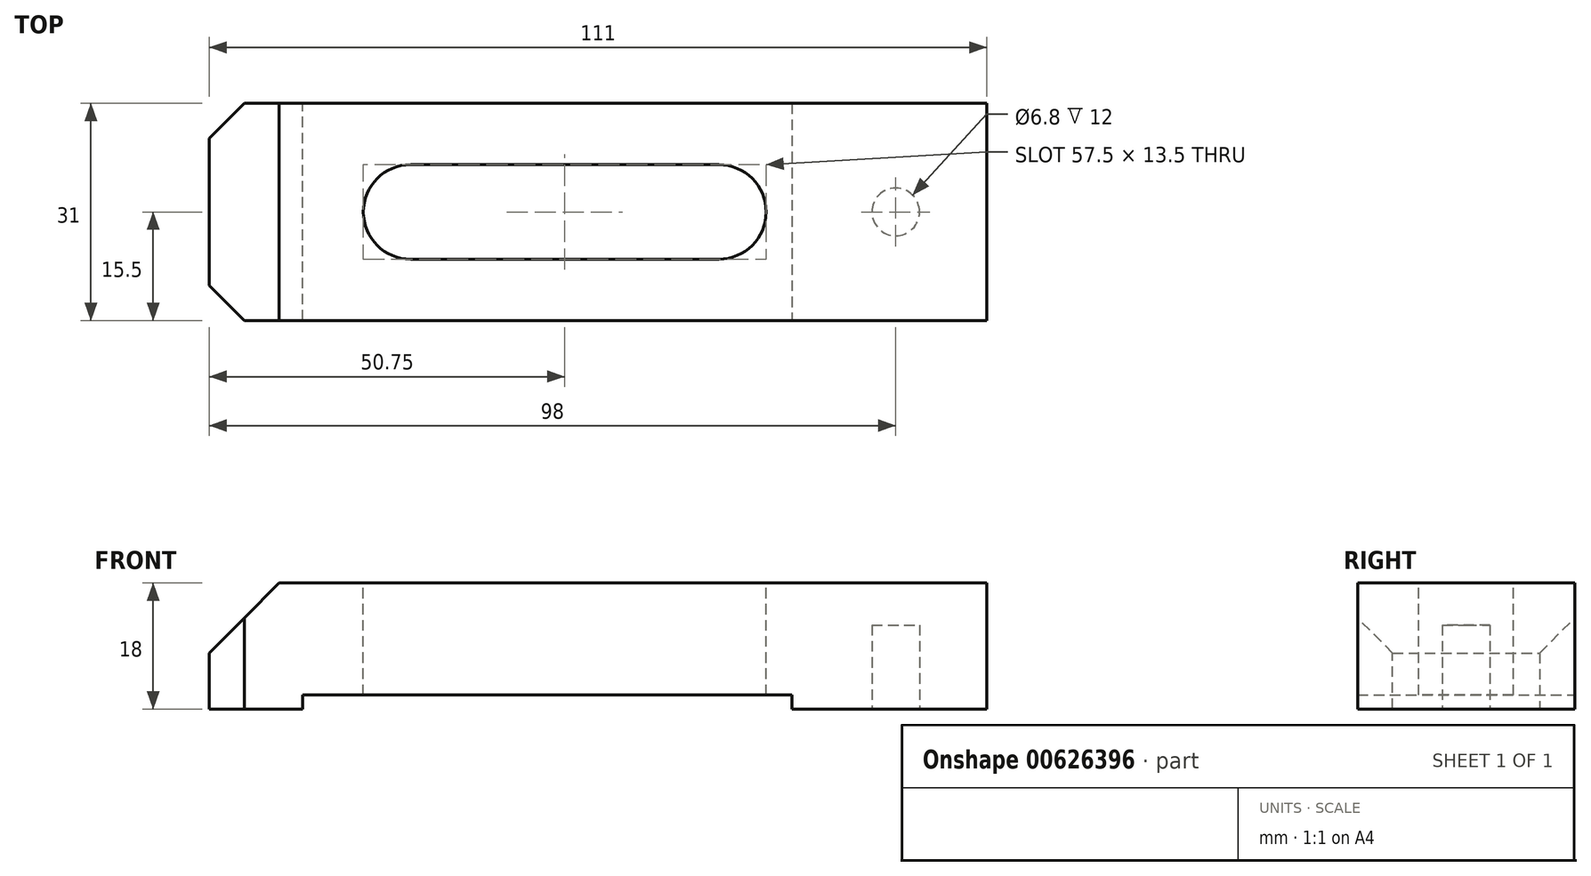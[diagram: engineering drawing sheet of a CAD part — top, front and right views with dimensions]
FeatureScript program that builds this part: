
annotation { "Feature Type Name" : "Feature", "Feature Type Description" : "" }
export const myFeature = defineFeature(function(context is Context, id is Id, definition is map)
    precondition{}
    {
        {
            var Q0;
            Q0=qCreatedBy(makeId("Top.planeOp"),FACE);
            var sketch = newSketch(context, id + "F0", { "sketchPlane" : qUnion([Q0])});
            skLineSegment(sketch, "E0.bottom", {"start": v(55.5, 15.5) * mm, "end": v(-55.5, 15.5) * mm});
            skLineSegment(sketch, "E0.top", {"start": v(55.5, -15.5) * mm, "end": v(-55.5, -15.5) * mm});
            skLineSegment(sketch, "E0.left", {"start": v(55.5, 15.5) * mm, "end": v(55.5, -15.5) * mm});
            skLineSegment(sketch, "E0.right", {"start": v(-55.5, 15.5) * mm, "end": v(-55.5, -15.5) * mm});
            skPoint(sketch, "E0.middle", {"position": v(0, 0) * mm});
            skSolve(sketch);
        }
        {
            var Q0;
            Q0=makeQuery(id+"F0.imprint","IMPRINT",FACE,{"disambiguationData":[TD([[makeQuery(id+"F0.imprint","IMPRINT",EDGE,{"derivedFrom":sQuery(id+"F0.wireOp",EDGE,"E0.bottom")}),1.0]])]});
            extrude(context, id + "F1", {"entities" : qUnion([Q0]), "depth" : 18 * mm, "offsetDistance" : 25 * mm});
        }
        {
            var Q0;
            Q0=makeQuery(id+"F1.opExtrude","CAP_FACE",FACE,{"disambiguationData":[OSD([sQuery(id+"F0.wireOp",EDGE,"E0.bottom"),sQuery(id+"F0.wireOp",EDGE,"E0.top"),sQuery(id+"F0.wireOp",EDGE,"E0.left"),sQuery(id+"F0.wireOp",EDGE,"E0.right")])],"isStart":false});
            var sketch = newSketch(context, id + "F2", { "sketchPlane" : qUnion([Q0])});
            skArc(sketch, "E1", {"start": v(-26.75, 6.75) * mm, "mid": v(-33.5, 0) * mm, "end": v(-26.75, -6.75) * mm});
            skArc(sketch, "E2", {"start": v(17.25, -6.75) * mm, "mid": v(24, 0) * mm, "end": v(17.25, 6.75) * mm});
            skLineSegment(sketch, "E3", {"start": v(-26.75, 6.75) * mm, "end": v(17.25, 6.75) * mm});
            skLineSegment(sketch, "E4", {"start": v(-26.75, -6.75) * mm, "end": v(17.25, -6.75) * mm});
            skSolve(sketch);
        }
        {
            var Q0;
            Q0=makeQuery(id+"F2.imprint","IMPRINT",FACE,{"disambiguationData":[TD([[makeQuery(id+"F2.imprint","IMPRINT",EDGE,{"derivedFrom":sQuery(id+"F2.wireOp",EDGE,"E1")}),1.0]])]});
            extrude(context, id + "F3", {"entities" : qUnion([Q0]), "operationType" : NewBodyOperationType.REMOVE, "oppositeDirection" : true, "depth" : 20 * mm, "offsetDistance" : 25 * mm});
        }
        {
            var Q0;
            Q0=makeQuery(id+"F1.opExtrude","CAP_FACE",FACE,{"disambiguationData":[OSD([sQuery(id+"F0.wireOp",EDGE,"E0.bottom"),sQuery(id+"F0.wireOp",EDGE,"E0.top"),sQuery(id+"F0.wireOp",EDGE,"E0.left"),sQuery(id+"F0.wireOp",EDGE,"E0.right")])],"isStart":true});
            var sketch = newSketch(context, id + "F4", { "sketchPlane" : qUnion([Q0])});
            skCircle(sketch, "E5", {"center": v(42.5, 0) * mm, "radius": 3.4 * mm});
            skSolve(sketch);
        }
        {
            var Q0;
            Q0=makeQuery(id+"F4.imprint","IMPRINT",FACE,{"disambiguationData":[TD([[makeQuery(id+"F4.imprint","IMPRINT",EDGE,{"derivedFrom":sQuery(id+"F4.wireOp",EDGE,"E5")}),1.0]])]});
            extrude(context, id + "F5", {"entities" : qUnion([Q0]), "operationType" : NewBodyOperationType.REMOVE, "oppositeDirection" : true, "depth" : 12 * mm, "offsetDistance" : 25 * mm});
        }
        {
            var Q0;
            Q0=makeQuery(id+"F1.opExtrude","CAP_FACE",FACE,{"disambiguationData":[OSD([sQuery(id+"F0.wireOp",EDGE,"E0.bottom"),sQuery(id+"F0.wireOp",EDGE,"E0.top"),sQuery(id+"F0.wireOp",EDGE,"E0.left"),sQuery(id+"F0.wireOp",EDGE,"E0.right")])],"isStart":true});
            var sketch = newSketch(context, id + "F6", { "sketchPlane" : qUnion([Q0])});
            skLineSegment(sketch, "E6", {"start": v(-42.15, 15.5) * mm, "end": v(-42.15, -15.5) * mm});
            skLineSegment(sketch, "E7", {"start": v(-42.15, -15.5) * mm, "end": v(27.69, -15.5) * mm});
            skLineSegment(sketch, "E8", {"start": v(27.69, -15.5) * mm, "end": v(27.69, 15.5) * mm});
            skLineSegment(sketch, "E9", {"start": v(27.69, 15.5) * mm, "end": v(-42.15, 15.5) * mm});
            skSolve(sketch);
        }
        {
            var Q0;
            Q0=makeQuery(id+"F6.imprint","IMPRINT",FACE,{"disambiguationData":[TD([[makeQuery(id+"F6.imprint","IMPRINT",EDGE,{"derivedFrom":sQuery(id+"F6.wireOp",EDGE,"E6")}),1.0]])]});
            extrude(context, id + "F7", {"entities" : qUnion([Q0]), "operationType" : NewBodyOperationType.REMOVE, "oppositeDirection" : true, "depth" : 2 * mm, "offsetDistance" : 25 * mm});
        }
        {
            var Q0;
            Q0=makeQuery(id+"F1.opExtrude","CAP_EDGE",EDGE,{"disambiguationData":[OSD([sQuery(id+"F0.wireOp",EDGE,"E0.right")])],"isStart":false});
            chamfer(context, id + "F8", {"entities" : qUnion([Q0]), "width" : 10 * mm, "tangentPropagation" : true});
        }
        {
            var Q0;
            Q0=makeQuery(id+"F1.opExtrude","SWEPT_EDGE",EDGE,{"disambiguationData":[OSD([sQuery(id+"F0.wireOp",EDGE,"E0.top"),sQuery(id+"F0.wireOp",EDGE,"E0.right")])]});
            var Q1;
            Q1=makeQuery(id+"F1.opExtrude","SWEPT_EDGE",EDGE,{"disambiguationData":[OSD([sQuery(id+"F0.wireOp",EDGE,"E0.bottom"),sQuery(id+"F0.wireOp",EDGE,"E0.right")])]});
            chamfer(context, id + "F9", {"entities" : qUnion([Q0, Q1]), "width" : 5 * mm, "tangentPropagation" : true});
        }
    });
